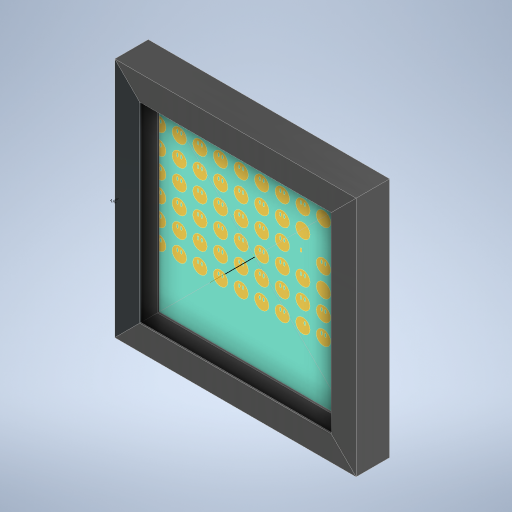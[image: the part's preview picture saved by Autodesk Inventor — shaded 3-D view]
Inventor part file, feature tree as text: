
AUTODESK INVENTOR PART (.ipt)
format: ipt  version: 2023 (Build 270158030, 158C)  size: 2,745,344 bytes
history: native  units: mm
features: extrude x22, sketch x20, projected_geometry x15, other x14, plane x3, pattern_circular x3, fillet x2, pattern_linear x1
ambient origin geometry x8: Origin, YZ Plane, XZ Plane, XY Plane, X Axis, Y Axis, Z Axis, Center Point
bodies: Solid10 (feature_tree), Solid11 (feature_tree), Solid12 (feature_tree), Solid13 (feature_tree), Solid14 (feature_tree), Solid15 (feature_tree), Solid16 (feature_tree), Solid17 (feature_tree), Solid18 (feature_tree)
feature tree (80):
  other  "art"
  extrude  "Extrusion1"  Depth=231.0mm
  extrude  "Extrusion2"  Depth=0.02mm TaperAngle=0.0deg
  extrude  "Extrusion3"  Depth=10.0mm
  extrude  "Extrusion4"  Depth=1.0mm
  extrude  "Extrusion6"  Depth=2.0mm
  extrude  "Extrusion10"  Depth=0.02mm TaperAngle=0.0deg
  extrude  "Extrusion11"  Depth=1.5mm
  extrude  "Extrusion12"  Depth=15.0mm
  sketch  "Sketch18"  dims[d34=2.0mm d35=0.0mm d39=1.5mm]
  extrude  "Extrusion13"  Depth=220.0mm
  extrude  "Extrusion18"  Depth=13.5mm
  plane  "Work Plane3"
  extrude  "Extrusion19"  Depth=5.5mm
  pattern_linear  "Rectangular Pattern1"  Count1=4 Spacing1=360.0deg
  fillet  "Fillet1"  Radius=3.0mm
  fillet  "Fillet2"  [1 undecoded]
  other  "Work Axis1"
  extrude  "Extrusion20"  Depth=15.0mm
  extrude  "Extrusion21"  Depth=13.0mm
  pattern_circular  "Circular Pattern5"  [2 undecoded]
  extrude  "Extrusion14"  Depth=10.0mm
  extrude  "Extrusion15"  Depth=10.0mm
  extrude  "Extrusion22"  Depth=1.5mm
  pattern_circular  "Circular Pattern6"  [2 undecoded]
  extrude  "Extrusion16"  Depth=25.0mm
  extrude  "Extrusion17"  Depth=25.0mm
  extrude  "Extrusion23"  Depth=25.0mm
  extrude  "Extrusion24"  Depth=2.0mm TaperAngle=0.0deg
  extrude  "Extrusion25"  Depth=2.0mm TaperAngle=0.0deg
  plane  "Work Plane4"
  sketch  "Sketch34"  dims[d109=2.0mm d110=0.0mm d113=15.0mm d116=13.0mm d118=6.0mm d122=2.0mm d123=0.0mm d133=10.0mm d134=10.0mm d136=10.0mm d139=1.5mm d142=1.51mm d143=25.0mm d144=25.0mm d145=25.0mm d146=25.0mm d147=2.0mm d148=0.0mm d149=2.0mm d150=0.0mm d152=35.0mm d153=0.0mm d155=1.5mm d156=0.0mm d157=4.5mm d159=15.0mm d160=7.5mm d165=2.0mm d166=0.0mm d167=12.0mm d168=12.0mm d169=12.0mm d170=7.0mm d171=7.5mm d172=2.5mm d173=2.0mm d174=0.0mm d175=20.0mm d177=23.0mm d178=30.0mm d180=55.0mm d181=1.0mm d182=2.0mm d183=3.0mm d184=45.0deg d185=0.7mm d186=0.0mm d190=45.0deg d191=3.0mm d192=0.7mm d193=0.0mm d197=40.0mm d198=360.0deg d204=10.0mm d205=90.0mm d207=21.5mm d208=90.0mm d210=21.5mm d213=0.0mm d214=0.0mm d215=40.0mm d216=360.0deg d218=50.0mm d219=0.0mm d224=1.0mm d225=0.0mm d226=15.0mm d227=15.0mm d228=1.0mm d229=0.0mm d230=1.0mm d231=202.0mm d232=0.0mm d235=40.0mm d236=360.0deg d238=7.5mm d239=7.5mm d240=4.5mm d241=6.0mm d243=7.5mm d244=1.51mm d245=1.51mm d246=1.51mm d247=1.5mm d248=1.51mm d249=1.51mm d250=1.51mm d251=1.51mm d252=26.0mm d253=26.51mm d254=26.0mm d255=26.0mm d256=26.0mm d257=15.0mm]
  extrude  "Extrusion26"  Depth=15.0mm TaperAngle=0.0deg
  pattern_circular  "Circular Pattern7"  [2 undecoded]
  sketch  "Sketch1"  dims[d0=231.0mm d1=231.0mm]
  sketch  "Sketch2"  dims[d2=0.01mm d3=0.0mm d8=0.02mm d9=0.0mm]
  sketch  "Sketch4"  dims[d10=15.0mm d12=10.0mm]
  other  "back-plate"
  sketch  "Sketch7"  dims[d15=1.0mm d16=1.0mm]
  projected_geometry  "Projected Loop9"
  sketch  "Sketch13"  dims[d17=2.0mm d18=2.0mm]
  projected_geometry  "Projected Loop17"
  sketch  "Sketch15"  dims[d19=3.0mm d28=0.02mm d29=0.0mm]
  projected_geometry  "Projected Loop18"
  sketch  "Sketch22"  dims[d40=10.0mm d41=0.0mm d42=15.0mm]
  projected_geometry  "Projected Loop20"
  other  "closure1"
  sketch  "Sketch23"  dims[d69=204.0mm d70=220.0mm]
  projected_geometry  "Projected Loop22"
  sketch  "Sketch24"  dims[d71=13.5mm d72=13.5mm]
  projected_geometry  "Projected Loop23"
  other  "outer"
  sketch  "Sketch25"  dims[d73=5.5mm d74=5.5mm]
  projected_geometry  "Projected Loop24"
  sketch  "Sketch26"  dims[d78=7.5mm]
  projected_geometry  "Projected Loop26"
  plane  "Work Plane2"
  sketch  "Sketch27"  dims[d80=7.5mm]
  projected_geometry  "Projected Loop27"
  projected_geometry  "Projected Loop28"
  projected_geometry  "Projected Loop29"
  sketch  "Sketch28"  dims[d82=15.0mm]
  sketch  "Sketch29"  dims[d83=15.0mm]
  other  "Pattern of back-plate:4"
  other  "Pattern of back-plate:5"
  other  "Pattern of back-plate:6"
  sketch  "Sketch30"  dims[d84=246.0mm]
  projected_geometry  "Projected Loop30"
  other  "Pattern of closure1:7"
  other  "Pattern of closure1:8"
  other  "Pattern of closure1:9"
  projected_geometry  "Projected Loop31"
  sketch  "Sketch31"  dims[d85=55.0mm]
  projected_geometry  "Projected Loop32"
  sketch  "Sketch32"  dims[d86=55.0mm]
  sketch  "Sketch33"  dims[d87=15.0mm d88=40.0mm d90=360.0deg d92=3.0mm d93=0.0mm d101=0.0mm d102=0.0mm]
  other  "Pattern of outer:10"
  other  "Pattern of outer:11"
  other  "Pattern of outer:12"
  projected_geometry  "Projected Loop33"
note: 7 required parameter values undecoded (feature->parameter linkage not recoverable at this tier; creation-order binding heuristic only, values carry confidence <= 0.55)
